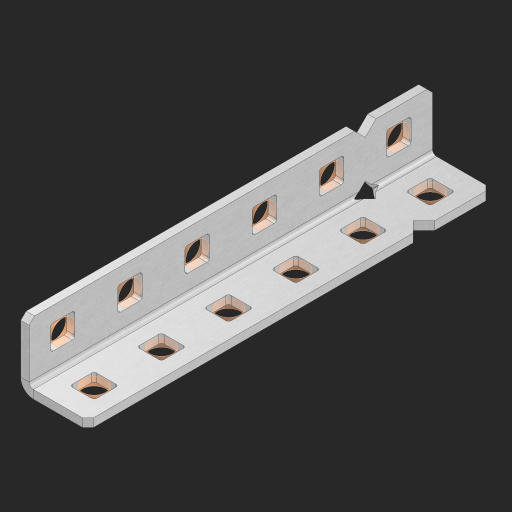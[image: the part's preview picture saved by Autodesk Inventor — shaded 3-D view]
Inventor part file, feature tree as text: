
AUTODESK INVENTOR PART (.ipt)
format: ipt  version: 2023 (Build 270158000, 158)  size: 541,184 bytes
history: native  units: in
note: dims shown in document units (in); Inventor stores cm internally (conversion verified against a paired STEP export)
features: other x18, extrude x13, sheet_metal_op x8, sketch x5, pattern_linear x1, mirror x1, chamfer x1
ambient origin geometry x8: Origin, YZ Plane, XZ Plane, XY Plane, X Axis, Y Axis, Z Axis, Center Point
bodies: Solid1 (feature_tree), Body (feature_tree)
feature tree (47):
  sheet_metal_op  "Flanges"
  sheet_metal_op  "Body Pattern"
  other  "Arc Length"
  pattern_linear  "Notch Pattern"  Spacing1=0.125in  [1 undecoded]
  other  "Diagonal Plane"
  mirror  "Everything Mirrored"
  chamfer  "End Chamfer"
  sketch  "Sketch1"  dims[d0=0.5in]
  other  "Plate1"
  sketch  "Sketch2"  dims[d1=3.0in]
  other  "Plate2"
  sheet_metal_op  "Bend1"
  sheet_metal_op  "Corner1"
  sketch  "Sketch8"  dims[d2=0.0625in]
  sketch  "Sketch9"  dims[d3=0.0625in]
  other  "Srf91"
  sheet_metal_op  "Body Pattern Sketch"
  other  "Srf92"
  sketch  "Sketch13"  dims[d4=0.0312in d5=0.125in d6=0.0625in d7=0.5in d8=90.0deg d9=0.0312in d10=0.25in d11=0.0625in d12=0.0625in d49=0.182in d50=0.02in d52=0.25in d53=0.0625in d54=0.0in d55=0.172in d56=1.0in d57=0.0in d85=0.1473in d86=0.1782in d89=0.0625in d90=0.0in d91=0.04in d92=0.0491in d95=2.5in d96=0.04in d97=0.25in d98=45.0deg d123=0.204in d126=0.0491in d127=0.1473in d128=0.08in d129=0.04in d130=2.5in d131=2.3622in d133=0.5in d134=0.3937in d136=1.0in]
  other  "Srf856"
  other  "Srf857"
  other  "Srf858"
  other  "Srf859"
  other  "Srf860"
  other  "Srf1275"
  other  "Srf1276"
  other  "Srf1278"
  other  "Srf1279"
  other  "Srf1280"
  other  "Srf1281"
  other  "Srf1282"
  sheet_metal_op  "Body Stamp"
  sheet_metal_op  "Body Circle"
  sheet_metal_op  "Notch"
  extrude  "ExtrusionSrf92"  Depth=0.0625in
  extrude  "ExtrusionSrf856"  Depth=0.5in TaperAngle=90.0deg
  extrude  "ExtrusionSrf857"  Depth=0.3937in
  extrude  "ExtrusionSrf858"  Depth=0.0625in
  extrude  "ExtrusionSrf859"  Depth=0.0625in
  extrude  "ExtrusionSrf860"  Depth=0.3937in
  extrude  "ExtrusionSrf1275"  Depth=0.02in
  extrude  "ExtrusionSrf1276"  Depth=0.3937in
  extrude  "ExtrusionSrf1277"  Depth=0.0625in
  extrude  "ExtrusionSrf1278"  TaperAngle=0.0deg  [1 undecoded]
  extrude  "ExtrusionSrf1279"  Depth=0.3937in
  extrude  "ExtrusionSrf1280"  Depth=0.3937in TaperAngle=0.0deg
  extrude  "ExtrusionSrf1281"  Depth=0.3937in
note: 2 required parameter values undecoded (feature->parameter linkage not recoverable at this tier; creation-order binding heuristic only, values carry confidence <= 0.55)
